# Revit family: Terminal_Unit-Carnes-AVED-Single_Duct-Rectangular
name_source: partatom
category: Mechanical Equipment
revit_build: Autodesk Revit MEP 2012 (Build: 20110309_2315(x64)
units: mm (PartAtom-declared; Revit-internal decimal feet)

## types (2) — shared parameters
04 CSI = 23 34 23
95 CSI = 15830
A = 32"
Airflow = 0.0 L/s
Amperage = 0 A
Apparent Load = 0 VA
Assembly Code = D3040200
B = 17 1/2"
C = 44 3/8"
Catalog URL = http://www.carnes.com
Default Elevation = 48"
Description = Single Duct Terminal Units
E = 38 1/2"
F = 17 5/8"
Frequency = 0 Hz
IOM Instructions URL = http://www.carnes.com
Inlet Height = 16"
Manufacturer = CARNES COMPANY
Manufacturer Fax = 608-845-6470
Material = Galvanized Steel
Modeling Numbering System = http://www.carnes.com
Number of Poles = 1
Phase = 1
Product Page URL = http://www.carnes.com
Spec Sheet URL = http://www.carnes.com
Subcategory = Air Volume Terminal Units
URL = http://www.carnes.com
Unit = Metal - Carnes - Steel
Voltage = 0 V
Wattage = 0 W
ecoScorecard Product Page = http://ecoscorecard.com
zero-valued in all types: Power Factor

## per-type parameters (varying)
| type | Electronic Min. CFM Range | Inlet Diameter | Inlet Width | Max CFM Range | Pneu. Min. CFM Range | Rated CFM |
| AVED 18 | ø or 800 - 2200 | 16x18 | 18" | 3300 - 5500 | ø or 1100 - 2200 | 5500 m³ |
| AVED 24 | ø or 1095 - 2920 | 16x24 | 24" | 4380 - 7300 | ø or 1480 - 2920 | 7300 m³ |

note: column(s) folded — value = type name in every type: Model

## geometry (parser evidence)
native form markers: Blend x2, Sweep x15
no freeform markers — native parametric forms only
